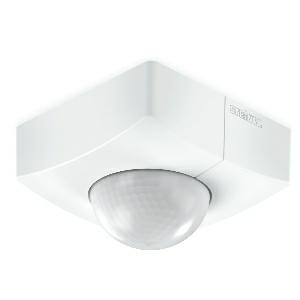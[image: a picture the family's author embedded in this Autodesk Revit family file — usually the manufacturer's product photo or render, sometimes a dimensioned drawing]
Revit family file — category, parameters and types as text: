
# Revit family: is_345_mx_highbay_058296
name_source: partatom
category: Elektroinstallationen
revit_build: Autodesk Revit 2016 (Build: 20190508_0715(x64)
units: mm (PartAtom-declared; Revit-internal decimal feet)

## family parameters
Basisbauteil = Fläche
Beim Laden mit Abzugskörper schneiden = Nein
Bemaßung runder Anschluss = Durchmesser verwenden
Beschriftungsausrichtung beibehalten = Nein
Gemeinsam genutzt = Nein
Raumberechnungspunkt = Nein
Teiletyp = Normal

## types (1)
- IS 345 MX Highbay
    Apparent Load = 0 VA
    Beschreibung = Type: Motion detectors; Dimensions (L x W x H): 65 x 95 x 95 mm; Power supply, detail: KNX bus; Sensor Technology: passive infrared; Application, place: Indoors; Application, room: high-bay warehouse, Indoors; Installation site: ceiling; Installation: Surface wiring; Electronic scalability: No; Mechanical scalability: No; Mounting height: 4,00 – 14,00 m; Optimum mounting height: 12 m; Detection angle: 360 °; Angle of aperture: 9 °; Sneak-by guard: Yes; Capability of masking out individual segments: Yes; Reach, radial: 30 x 4 m (120 m²); Reach, tangential: 30 x 4 m (120 m²); Twilight setting TEACH: Yes; Twilight setting: 2 – 1000 lx; Time setting: 0 sec – 1092 min; Basic light level function: Yes; KNX functions: Photo-cell controller, Basic light level function, Light level, HVAC output, Constant-lighting control, Light output 2x, Presence output, Day / night function; With bus coupling: Yes; Settings via: ETS software, Remote control, Bus, Smart Remote; IP-rating: IP54; Material: Plastic; Colour: white; Colour, RAL: 9003; Manufacturer's Warranty: 5 years; Version: KNX - surface, sq.; PU1, EAN: 4007841058296
    Height = 95 mm
    Hersteller = Steinel
    Length = 65 mm
    Maximum range = 3.441 m
    ModVariant = Nein
    Modell = 058296
    Mounting Place = Ceiling
    Mounting Type = Surface mounted
    Number of Poles = 1
    OnlyDefault = Ja
    Power Factor = 1
    Product Name = IS 345 MX Highbay
    Product group = Sensor-switched outdoor light
    ProductGroupID = 3
    Protection Class = Protection class
    Protection Degree = IP 54
    RlxData = <blob elided: 195141 chars, md5=6a97824c>
    Sensor characteristics = Circular 300°-360°
    Sensor type = Passive (infrared)
    SensorDataFile = <blob elided: 170895 chars, md5=da062800>
    Type of entry = Motion
    Typenbild = produkt1_058296.jpg
    Typenkommentare = Product without accessories
    URL = http://relux.com
    VarID = ---
    Voltage = 0 V
    Vorgabe-Ansicht = 1800 mm
    Weight = 0.00 kg
    Width = 95 mm

## geometry (parser evidence)
native form markers: Sweep x16
no freeform markers — native parametric forms only
